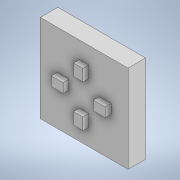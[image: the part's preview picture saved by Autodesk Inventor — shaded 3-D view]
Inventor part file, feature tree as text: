
AUTODESK INVENTOR PART (.ipt)
format: ipt  version: 2021 (Build 250183000, 183)  size: 129,024 bytes
history: native  units: in
note: dims shown in document units (in); Inventor stores cm internally (conversion verified against a paired STEP export)
features: extrude x2, sketch x2
ambient origin geometry x8: Origin, YZ Plane, XZ Plane, XY Plane, X Axis, Y Axis, Z Axis, Center Point
bodies: Solid1 (feature_tree)
feature tree (4):
  extrude  "Extrusion1"  Depth=0.5906in
  extrude  "Extrusion2"  Depth=0.0394in
  sketch  "Sketch1"  dims[d0=0.5906in d1=0.5906in]
  sketch  "Sketch2"  dims[d2=0.1181in d3=0.0in d4=0.1024in d5=0.0315in d6=0.0787in d7=0.063in d8=0.1024in d9=0.0315in d10=0.0787in d11=0.063in d12=0.1024in d13=0.0787in d14=0.1024in d15=0.0787in d16=0.0394in d17=0.0in]
